# Revit family: SCP
name_source: partatom
category: Communication Devices
units: mm (PartAtom-declared; Revit-internal decimal feet)

## family parameters
Cut with Voids When Loaded = No
Host = Face
Maintain Annotation Orientation = No
OmniClass Number = 23.85.80.11.27
OmniClass Title = Lighting Controls
Part Type = Normal
Room Calculation Point = No
Round Connector Dimension = Use Diameter
Shared = No

## types (2) — shared parameters
Assembly Code = D5020280
Certification = All electrical components shall be U.L.
recognized
Default Elevation = 48 "
Description = AAL's Sensor Control Programmable (SCP) accessory enables dimmable pole mounted luminaires to meet CA Title 24 requirements. The SCP is field-adjustable for post installation tuning, and is compatible with straight round poles, straight square poles, and fluted poles.
Features = CA Title 24 Solution
• Motion Sensing up to 40' mounting height
• Daylight Photo Control
• 0-10V Control Signal
1. MODEL
Standard daylight photo-control with motion
sensing coverage up to 40' sensor height.
SCP 120-277 VAC
SCP-HV3 347 VAC
SCP-HV4 480 VAC
2. POLE
The SCP may be ordered as an accessory to
a configured pole or in the case of a stand
alone unit, the pole contour must be
communicated to the factory.
R3 fits a 3" / 76.2 mm round pole
R4 fits a 4" / 101.6 mm round pole
R5 fits a 5" / 127 mm round pole
S fits a square pole
Model Pole Color Remote
SPECIFICATIONS
• 20KV/10KA Surge Protection
• Hand Held Remote Adjustment
• For Round or Square Straight Poles
• AAL Poles include wire and mounting holes
Finish = Black
Glass = Glass
IP Rating = IP66
Manufacturer = Architectural Area Lighting
Model = Sensor Control Programmable – SCP
URL = https://www.currentlighting.com

## per-type parameters (varying)
| type | Length | Sensor Position |
| SCP | 5.75 " | 3.9 " |
| SCP-HV3/SCP-HV4 | 11 " | 9.15 " |

## geometry (parser evidence)
native form markers: Blend x1, Sweep x3
no freeform markers — native parametric forms only
